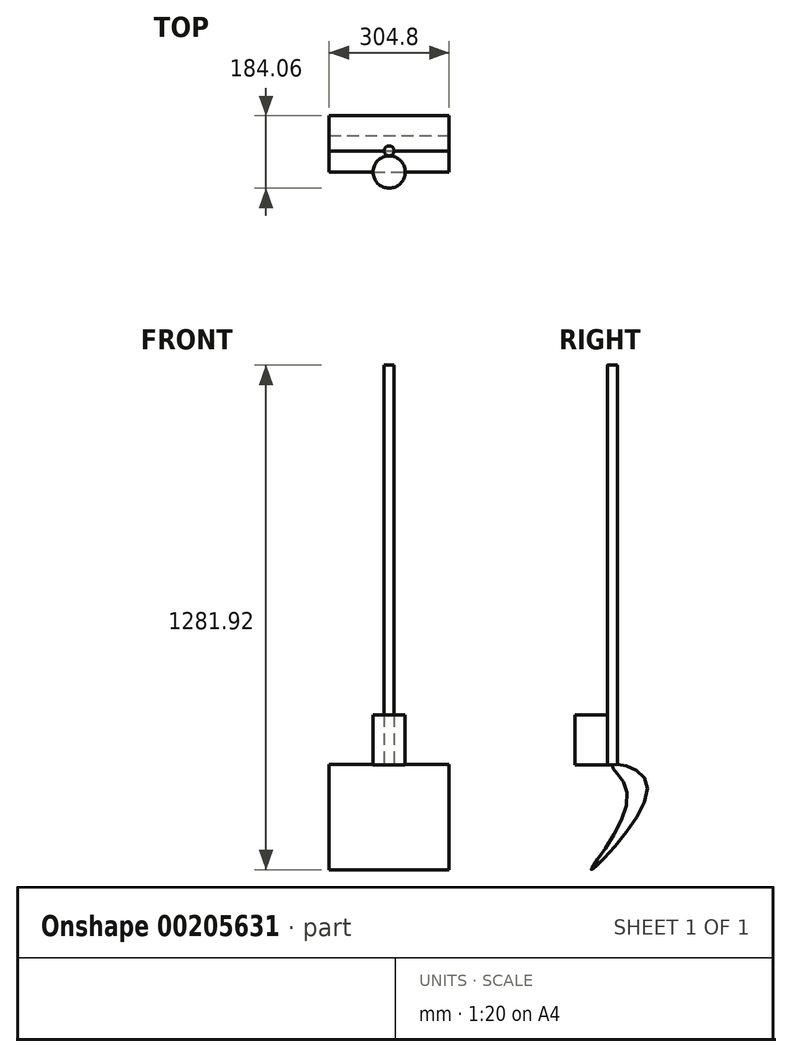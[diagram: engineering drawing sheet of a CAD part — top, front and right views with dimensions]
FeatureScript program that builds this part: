
annotation { "Feature Type Name" : "Feature", "Feature Type Description" : "" }
export const myFeature = defineFeature(function(context is Context, id is Id, definition is map)
    precondition{}
    {
        {
            var Q0;
            Q0=qCreatedBy(makeId("Top.planeOp"),FACE);
            var sketch = newSketch(context, id + "F0", { "sketchPlane" : qUnion([Q0])});
            skCircle(sketch, "E0", {"center": v(0, 0) * mm, "radius": 12.7 * mm});
            skSolve(sketch);
        }
        {
            var Q0;
            Q0 = qSketchRegion(id + "F0", true);
            extrude(context, id + "F1", {"entities" : qUnion([Q0]), "depth" : 1016 * mm});
        }
        {
            var Q0;
            Q0=qCreatedBy(makeId("Right.planeOp"),FACE);
            var sketch = newSketch(context, id + "F2", { "sketchPlane" : qUnion([Q0])});
            skFitSpline(sketch, "E1", {"points": [v(0, 0) * mm, v(88.36, -47.6) * mm, v(-53.36, -265.92) * mm, v(38.56, -78.24) * mm, v(0, 0) * mm]});
            skSolve(sketch);
        }
        {
            var Q0;
            Q0=makeQuery(id+"F2.imprint","IMPRINT",FACE,{"disambiguationData":[TD([[makeQuery(id+"F2.imprint","IMPRINT",EDGE,{"derivedFrom":sQuery(id+"F2.wireOp",EDGE,"E1")}),-1.0]])]});
            extrude(context, id + "F3", {"entities" : qUnion([Q0]), "operationType" : NewBodyOperationType.ADD, "depth" : 152.4 * mm, "hasSecondDirection" : true, "secondDirectionOppositeDirection" : true, "secondDirectionDepth" : 152.4 * mm});
        }
        {
            var Q0;
            Q0=qCreatedBy(makeId("Top.planeOp"),FACE);
            var sketch = newSketch(context, id + "F4", { "sketchPlane" : qUnion([Q0])});
            skCircle(sketch, "E2", {"center": v(0, -53.9) * mm, "radius": 40.87 * mm});
            skSolve(sketch);
        }
        {
            var Q0;
            Q0 = qSketchRegion(id + "F4", true);
            extrude(context, id + "F5", {"entities" : qUnion([Q0]), "operationType" : NewBodyOperationType.ADD, "depth" : 127 * mm});
        }
    });
